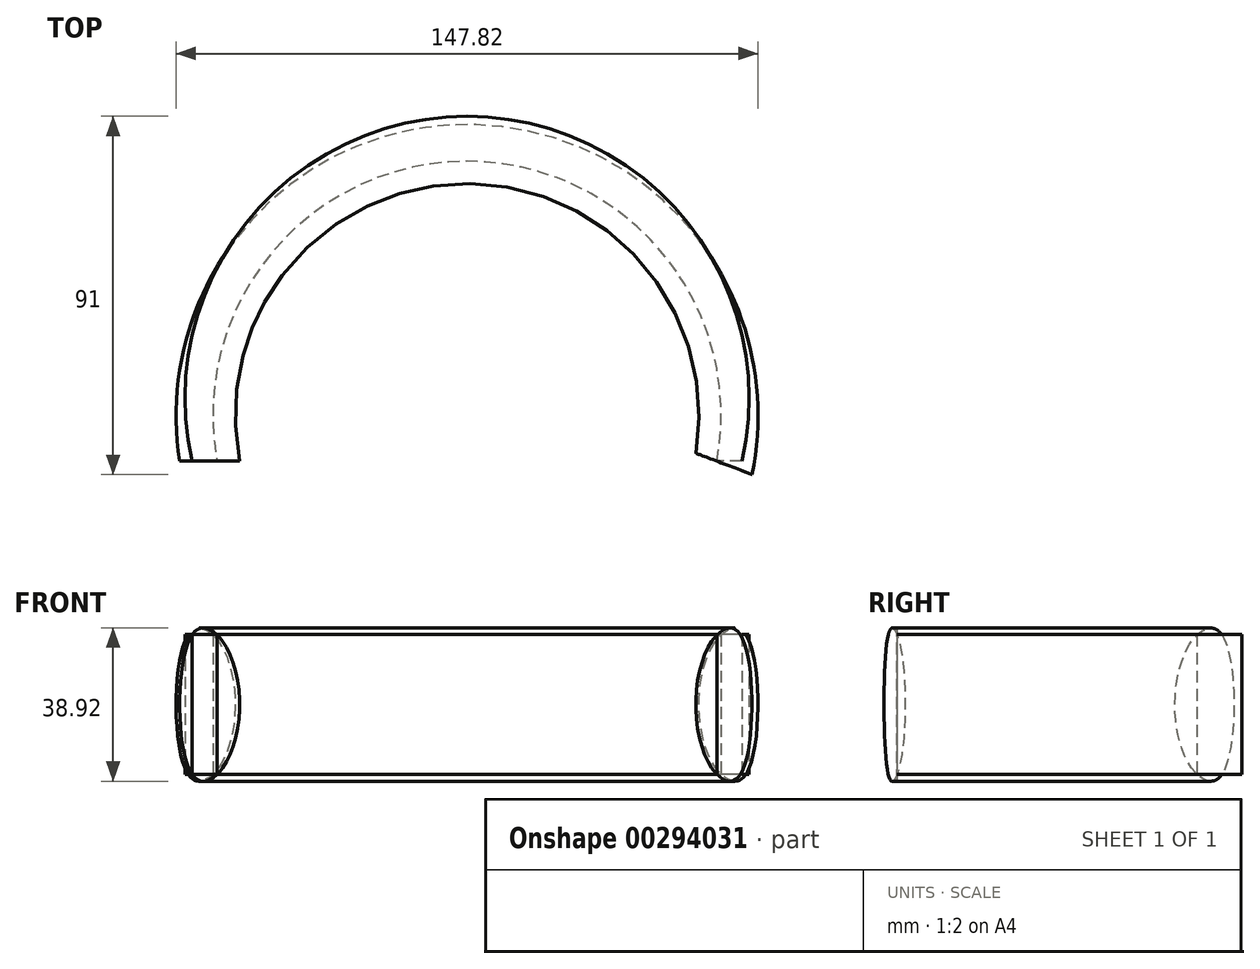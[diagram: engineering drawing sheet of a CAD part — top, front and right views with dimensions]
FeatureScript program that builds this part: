
annotation { "Feature Type Name" : "Feature", "Feature Type Description" : "" }
export const myFeature = defineFeature(function(context is Context, id is Id, definition is map)
    precondition{}
    {
        {
            var Q0;
            Q0=qCreatedBy(makeId("Top.planeOp"),FACE);
            var sketch = newSketch(context, id + "F0", { "sketchPlane" : qUnion([Q0])});
            skArc(sketch, "E0", {"start": v(63.5, 0) * mm, "mid": v(0, 76.2) * mm, "end": v(-63.5, 0) * mm});
            skArc(sketch, "E1", {"start": v(69.85, 0) * mm, "mid": v(0, 87.63) * mm, "end": v(-69.85, 0) * mm});
            skLineSegment(sketch, "E2", {"start": v(-63.5, 0) * mm, "end": v(-69.85, 0) * mm});
            skLineSegment(sketch, "E3", {"start": v(69.85, 0) * mm, "end": v(63.5, 0) * mm});
            skSolve(sketch);
        }
        {
            var Q0;
            Q0 = qSketchRegion(id + "F0", true);
            extrude(context, id + "F1", {"entities" : qUnion([Q0]), "depth" : 35.56 * mm});
        }
        {
            var Q0;
            Q0=qCreatedBy(makeId("Front.planeOp"),FACE);
            var sketch = newSketch(context, id + "F2", { "sketchPlane" : qUnion([Q0])});
            skFitSpline(sketch, "E4", {"points": [v(-69.85, 35.56) * mm, v(-63.5, 35.56) * mm, v(-57.75, 17.78) * mm, v(-63.5, 0) * mm, v(-69.85, 0) * mm, v(-69.85, 35.56) * mm]});
            skPoint(sketch, "E5", {"position": v(-72.99, 17.78) * mm});
            skSolve(sketch);
        }
        {
            var Q0;
            Q0 = qSketchRegion(id + "F2", true);
            var Q1;
            Q1=makeQuery(id+"F1.opExtrude","CAP_EDGE",EDGE,{"disambiguationData":[OSD([sQuery(id+"F0.wireOp",EDGE,"E0")])],"isStart":false});
            sweep(context, id + "F3", {"profiles" : qUnion([Q0]), "path" : qUnion([Q1])});
        }
    });
